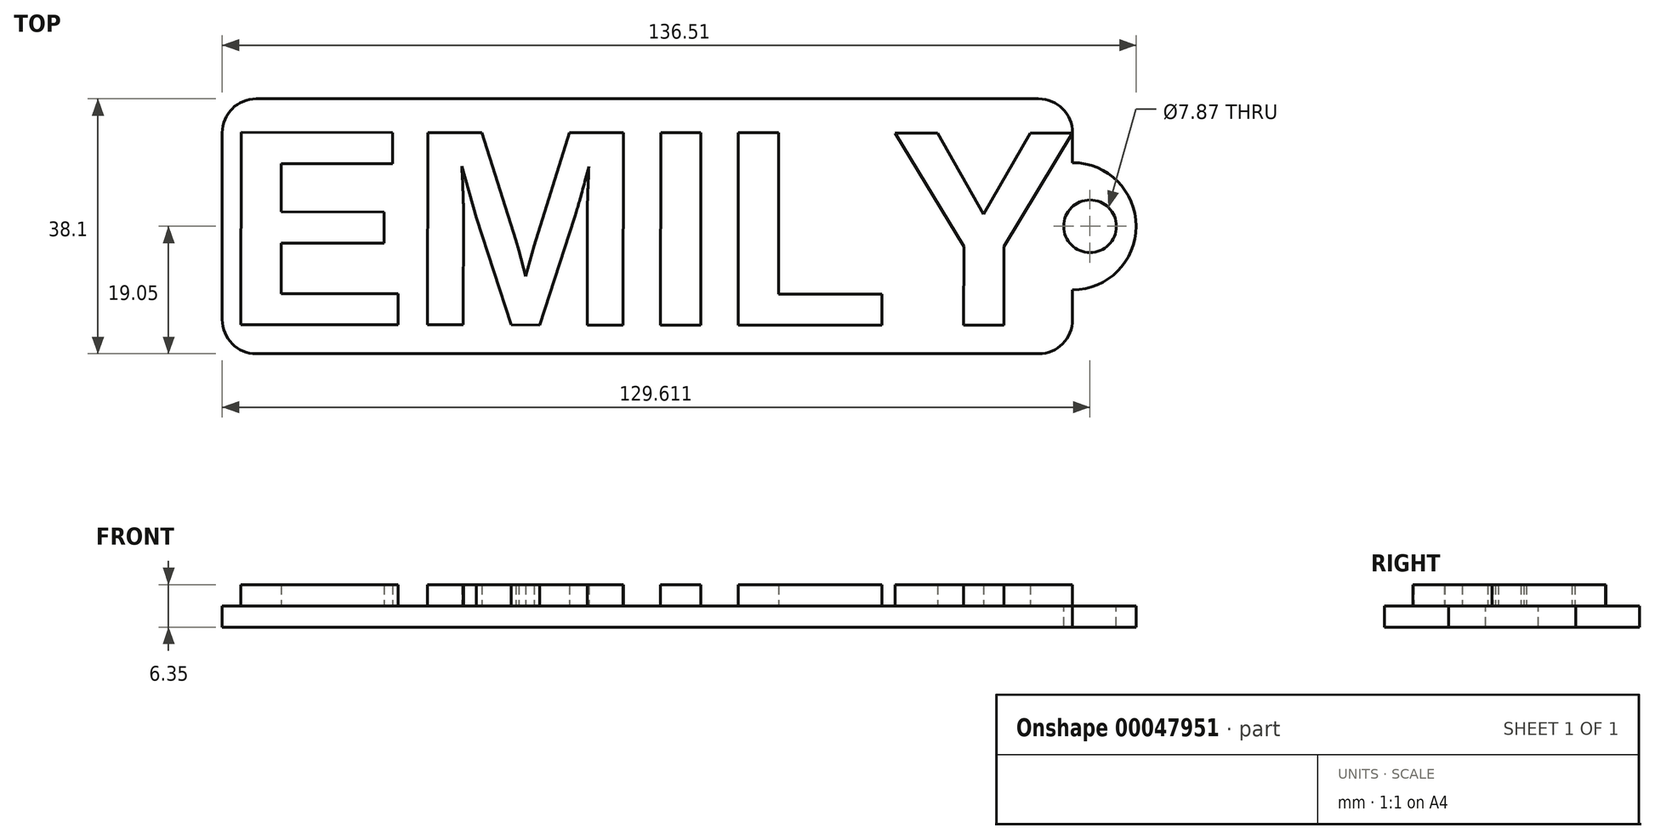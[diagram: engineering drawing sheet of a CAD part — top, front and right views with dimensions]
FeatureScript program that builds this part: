
annotation { "Feature Type Name" : "Feature", "Feature Type Description" : "" }
export const myFeature = defineFeature(function(context is Context, id is Id, definition is map)
    precondition{}
    {
        {
            var Q0;
            Q0=qCreatedBy(makeId("Top.planeOp"),FACE);
            var sketch = newSketch(context, id + "F0", { "sketchPlane" : qUnion([Q0])});
            skLineSegment(sketch, "E0.rect.bottom", {"start": v(63.5, 19.05) * mm, "end": v(-63.5, 19.05) * mm});
            skLineSegment(sketch, "E0.rect.top", {"start": v(63.5, -19.05) * mm, "end": v(-63.5, -19.05) * mm});
            skLineSegment(sketch, "E0.rect.left", {"start": v(63.5, 19.05) * mm, "end": v(63.5, -19.05) * mm});
            skLineSegment(sketch, "E0.rect.right", {"start": v(-63.5, 19.05) * mm, "end": v(-63.5, -19.05) * mm});
            skPoint(sketch, "E0.rect.middle", {"position": v(0, 0) * mm});
            skSolve(sketch);
        }
        {
            var Q0;
            Q0=makeQuery(id+"F0.imprint","IMPRINT",FACE,{"disambiguationData":[TD([[makeQuery(id+"F0.imprint","IMPRINT",EDGE,{"derivedFrom":sQuery(id+"F0.wireOp",EDGE,"E0.rect.bottom")}),1.0]])]});
            extrude(context, id + "F1", {"entities" : qUnion([Q0]), "depth" : 3.17 * mm});
        }
        {
            var Q0;
            Q0=makeQuery(id+"F1.opExtrude","CAP_FACE",FACE,{"disambiguationData":[OSD([sQuery(id+"F0.wireOp",EDGE,"E0.rect.bottom"),sQuery(id+"F0.wireOp",EDGE,"E0.rect.top"),sQuery(id+"F0.wireOp",EDGE,"E0.rect.left"),sQuery(id+"F0.wireOp",EDGE,"E0.rect.right")])],"isStart":false});
            var sketch = newSketch(context, id + "F2", { "sketchPlane" : qUnion([Q0])});
            skText(sketch, "E1", { "text": "EMILY", "fontName": "Arimo-Bold.ttf"});
            const initialGuessF2  = {"E1": [-0.0635, -0.01471, 1, -0.00085, 0.03008]};
            skSetInitialGuess(sketch, initialGuessF2);
            skSolve(sketch);
        }
        {
            var Q0;
            Q0 = qSketchRegion(id + "F2", true);
            extrude(context, id + "F3", {"entities" : qUnion([Q0]), "operationType" : NewBodyOperationType.ADD, "depth" : 3.17 * mm});
        }
        {
            var Q0;
            Q0=makeQuery(id+"F1.opExtrude","SWEPT_EDGE",EDGE,{"disambiguationData":[OSD([sQuery(id+"F0.wireOp",EDGE,"E0.rect.bottom"),sQuery(id+"F0.wireOp",EDGE,"E0.rect.right")])]});
            var Q1;
            Q1=makeQuery(id+"F1.opExtrude","SWEPT_EDGE",EDGE,{"disambiguationData":[OSD([sQuery(id+"F0.wireOp",EDGE,"E0.rect.top"),sQuery(id+"F0.wireOp",EDGE,"E0.rect.right")])]});
            var Q2;
            Q2=makeQuery(id+"F1.opExtrude","SWEPT_EDGE",EDGE,{"disambiguationData":[OSD([sQuery(id+"F0.wireOp",EDGE,"E0.rect.top"),sQuery(id+"F0.wireOp",EDGE,"E0.rect.left")])]});
            var Q3;
            Q3=makeQuery(id+"F1.opExtrude","SWEPT_EDGE",EDGE,{"disambiguationData":[OSD([sQuery(id+"F0.wireOp",EDGE,"E0.rect.bottom"),sQuery(id+"F0.wireOp",EDGE,"E0.rect.left")])]});
            fillet(context, id + "F4", {"entities" : qUnion([Q0, Q1, Q2, Q3]), "radius" : 5.08 * mm, "tangentPropagation" : true, "allowEdgeOverflow" : false});
        }
        {
            var Q0;
            Q0=makeQuery(id+"F1.opExtrude","CAP_FACE",FACE,{"disambiguationData":[OSD([sQuery(id+"F0.wireOp",EDGE,"E0.rect.bottom"),sQuery(id+"F0.wireOp",EDGE,"E0.rect.top"),sQuery(id+"F0.wireOp",EDGE,"E0.rect.left"),sQuery(id+"F0.wireOp",EDGE,"E0.rect.right")])],"isStart":true});
            var sketch = newSketch(context, id + "F5", { "sketchPlane" : qUnion([Q0])});
            skCircle(sketch, "E2", {"center": v(63.5, 0) * mm, "radius": 9.5 * mm});
            skSolve(sketch);
        }
        {
            var Q0;
            Q0 = qSketchRegion(id + "F5", true);
            extrude(context, id + "F6", {"entities" : qUnion([Q0]), "operationType" : NewBodyOperationType.ADD, "oppositeDirection" : true, "depth" : 3.17 * mm});
        }
        {
            var Q0;
            Q0=makeQuery(id+"F6.boolean.opBoolean","MERGE",FACE,{"derivedFrom":[makeQuery(id+"F1.opExtrude","CAP_FACE",FACE,{"disambiguationData":[OSD([sQuery(id+"F0.wireOp",EDGE,"E0.rect.bottom"),sQuery(id+"F0.wireOp",EDGE,"E0.rect.top"),sQuery(id+"F0.wireOp",EDGE,"E0.rect.left"),sQuery(id+"F0.wireOp",EDGE,"E0.rect.right")])],"isStart":false}),makeQuery(id+"F6.opExtrude","CAP_FACE",FACE,{"disambiguationData":[OSD([sQuery(id+"F5.wireOp",EDGE,"E2")])],"isStart":false})]});
            var sketch = newSketch(context, id + "F7", { "sketchPlane" : qUnion([Q0])});
            skCircle(sketch, "E3", {"center": v(66.11, 0) * mm, "radius": 3.93 * mm});
            skPoint(sketch, "E3.centerSnap0", {"position": v(73, 0) * mm});
            skSolve(sketch);
        }
        {
            var Q0;
            Q0 = qSketchRegion(id + "F7", true);
            extrude(context, id + "F8", {"entities" : qUnion([Q0]), "operationType" : NewBodyOperationType.REMOVE, "oppositeDirection" : true, "depth" : 25.4 * mm});
        }
    });
